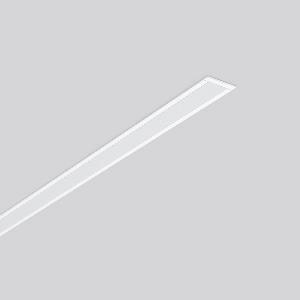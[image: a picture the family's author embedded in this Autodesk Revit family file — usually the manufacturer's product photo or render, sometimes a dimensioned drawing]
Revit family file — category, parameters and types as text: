
# Revit family: less_is_more_27_312176_002_1_965f
name_source: partatom
category: Lighting Fixtures
units: mm (PartAtom-declared; Revit-internal decimal feet)

## family parameters
Cut with Voids When Loaded = No
Host = Face
Light Source = No
Part Type = Normal
Room Calculation Point = No
Round Connector Dimension = Use Diameter
Shared = No

## types (1)
- LESS IS MORE 27 (1 x LED Modul 840, 1950 lm, 4000)
    Apparent Load = 25 VA
    CIE Flux Codes = 48 79 96 100 100
    Color Rendering = 80
    Color Temperature = 4000
    Default Elevation = 1800 mm
    Description = Series: LESS IS MORE 27
Recessed ceiling and wall luminaire with slim design. Housing: extruded aluminium profile, powder-coated. End cap aluminium powder-coated. Diffuser made of non-yellowing plastic (PMMA), opal. Suitable for Recessed ceiling mounting, wall (recessed). External driver with connecting cable. 
Colour: traffic white, matt (RAL 9016)
Length: 1014 mm
Width: 38 mm
Height: 2 mm
Cut-out length: 1006 mm
Cut-out width: 30 mm
Recess height: 45-60 mm
Luminaire: recess height: 37 mm
Lamp: LED
Socket: without socket
Colour temperature: 4000K
Colour rendering index (CRI): 82
System power: 25 W
Rated luminous flux: 1950 lm
Luminous efficiency: 78 lm/W
Control gear: Regulated power supply
Protection class: II
Type of protection: IP 20
    Height = 0 mm  [stored 0 ft]
    Lamp = 1 x LED Modul 840
    Lamp Light Flux = 1950 lm
    Lamp count = 1
    Length = 1014 mm
    Lifetime = 50000 h
    Luminous efficacy = 78 lm/W
    Manufacturer = RZB
    ModVariant = No
    Model = 312176.002.1
    Mounting Place = Ceiling, Wall
    Mounting Type = Recessed
    Number of Poles = 1
    OnlyDefault = Yes
    Power Factor = 1
    Product Name = LESS IS MORE 27
    Product group = Recessed LED linear luminaires
    ProductGroupID = 407
    Protection Class = Protection class II
    Protection Degree = IP 20
    RLX_Detail_Level = 1
    RLX_Emergency_Light_Flux = 0 lm
    RLX_Emergency_Type = 0
    RLX_Emergency_Type_DB = No
    RlxData = <blob elided: 21557 chars, md5=91cd9632>
    Socket = socket
    Standby Power = 0 W
    System Light Flux = 1950 lm
    System Power = 25 W
    Type Comments = Product without accessories
    Type Image = 312176.002.jpg
    URL = http://relux.com
    VarID = ---
    Voltage = 230 V
    Voltage Range = 220-240 V
    Weight = 0.00 kg
    Width = 38 mm

note: [stored X ft] marks values corroborated as IEEE doubles in the binary element streams (Revit-internal decimal feet)

## geometry (parser evidence)
native form markers: Blend x4, Sweep x11
no freeform markers — native parametric forms only
